# Revit family: 1Lighting_Pendant-Lighting_Molto-Luce_Ride-Recessed-Flat
name_source: partatom
category: Lighting Fixtures
revit_build: Autodesk Revit 2018 (Build: 20170223_1515(x64)
units: mm (PartAtom-declared; Revit-internal decimal feet)

## family parameters
Cut with Voids When Loaded = No
Host = Face
Light Source = Yes
OmniClass Number = 23.80.70.00
OmniClass Title = Lighting
Part Type = Normal
Room Calculation Point = No
Round Connector Dimension = Use Diameter
Shared = No

## types (1)
- Default - please load Revit Family Type Catalog
    BIMobject category = Pendant Lighting
    Color Filter = 16777215
    Connector Location = 2049 mm
    Default Elevation = 1219 mm
    Description = Ride Ring – the perfect addition to the Ride product family. With a profile of only 35x35 mm, this luminaire is one of the slimmest LED lighting systems currently on the market. The ring is available as a pendant or surface luminaire in two diameters, 750 mm and 1450 mm. The converter built into the body creates a minimalist ceiling base, which perfects the lighting effect down to the tiniest detail. There is a choice of black, white and silver powder coated colours. To use Ride Ring as system luminaire as well, a 90° and 180° circular segment is available in the two diameters, which can be variably connected variably, with or without the relevant linear profiles to create a variaty of shapes . Planners and architects can give their creativity free rein with this system. With Ride Ring as an individual luminaire or in a system, different project requirements can be optimally covered.
    Design country = Austria
    Dimming Lamp Color Temperature Shift = <None>
    Edition number = 1
    Emit from Line Length = 4217 mm  [stored 13.8353 ft]
    Housing Color = Molto Luce - Black
    IFC Classification = Lamp
    Installation instructions = https://www.moltoluce.com
    Length 1137 mm = No
    Length 1417 mm = No
    Length 2817 mm = No
    Length 4217 mm = Yes
    Length 577 mm = No
    Length 857 mm = No
    Light Source Symbol Size = 610 mm
    Manufacturer = Molto Luce
    Manufacturer country = Austria
    Manufacturer name = Molto Luce
    Masterformat 2014 Code = 26 50 00
    Masterformat 2014 Description = Lighting
    Material main = Aluminium
    Material secondary = Acrylic
    Model = Ride Recessed Flat
    NBS Reference Code = 49
    NBS Reference Description = Luminaires And Lamps
    OmniClass Code = 23-35 45 15
    OmniClass Description = Lamps
    Product Guid = 7360fe32-6db8-48d1-b030-d1c6f90c4fcb
    Product SKU = Ride_Recessed_Flat
    Product data url = https://bimobject.com
    Product family = Lighting
    Product group = Pendant Lamp
    Product name = Ride Recessed Flat
    QR code = https://bimobject.com
    UNSPSC Code = 3911
    URL = https://www.moltoluce.com
    Uniclass 1.4 Code = JY73
    Uniclass 1.4 Description = Luminaires and lamps
    Uniclass 2.0 Code = PR-49
    Uniclass 2.0 Description = Luminaires And Lamps
    Uniclass 2015 Code = Pr_70_70_48
    Uniclass 2015 Name = Luminaires, lighting track and lighting accessories
    Uniformat II Code = D5020
    Uniformat II Description = Lighting & Branch Wiring

note: [stored X ft] marks values corroborated as IEEE doubles in the binary element streams (Revit-internal decimal feet)

## geometry (parser evidence)
native form markers: Sweep x3
no freeform markers — native parametric forms only
